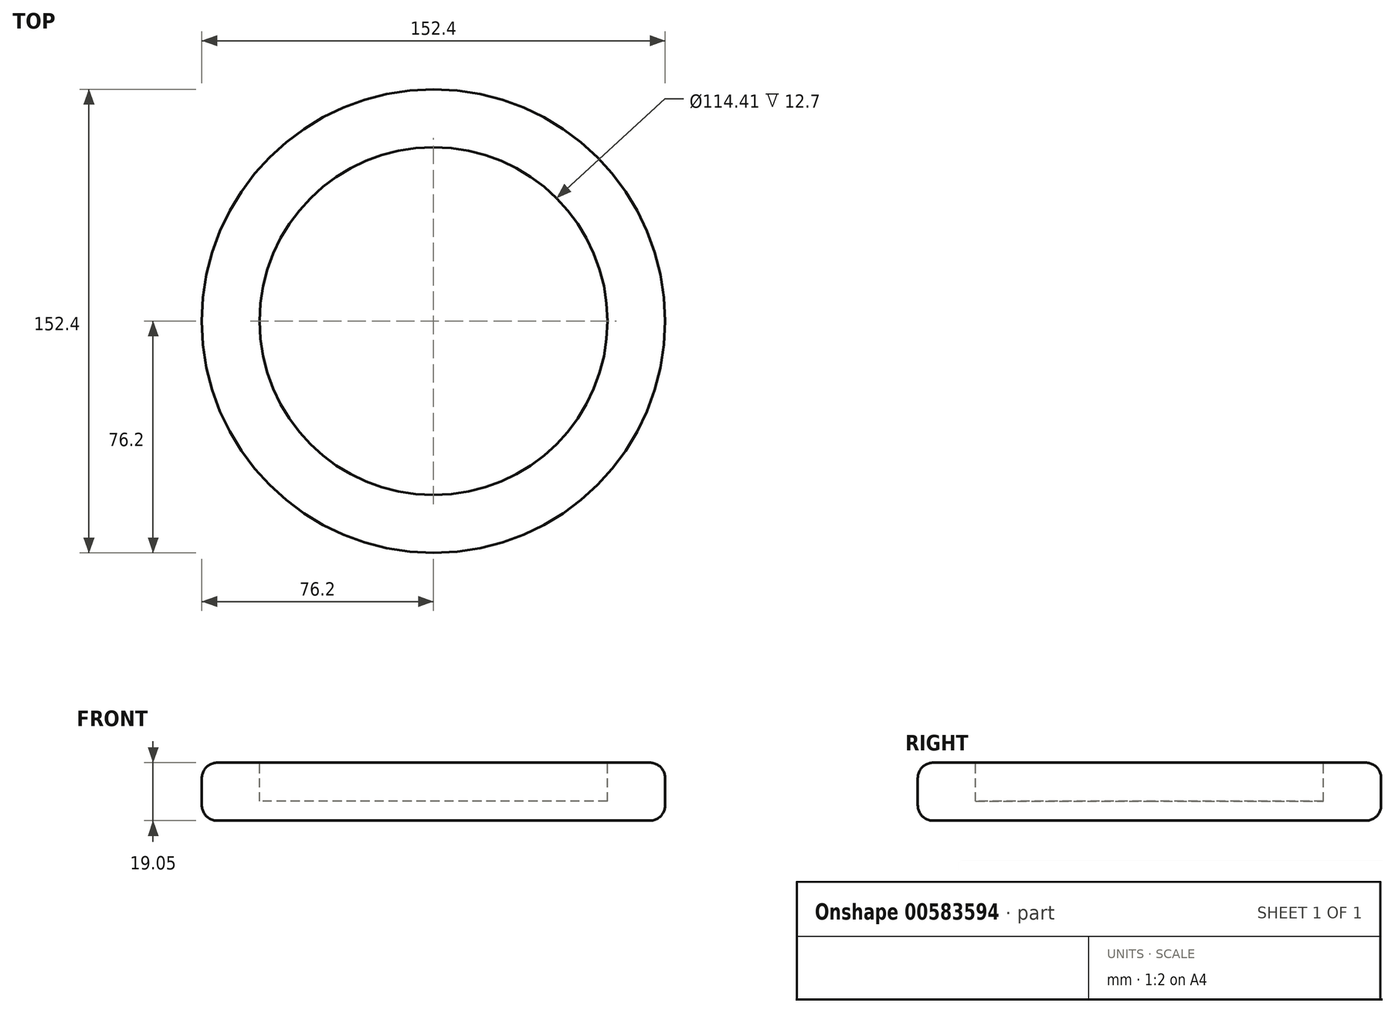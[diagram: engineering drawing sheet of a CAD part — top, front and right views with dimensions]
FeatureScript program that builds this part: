
annotation { "Feature Type Name" : "Feature", "Feature Type Description" : "" }
export const myFeature = defineFeature(function(context is Context, id is Id, definition is map)
    precondition{}
    {
        {
            var Q0;
            Q0=qCreatedBy(makeId("Top.planeOp"),FACE);
            var sketch = newSketch(context, id + "F0", { "sketchPlane" : qUnion([Q0])});
            skCircle(sketch, "E0", {"center": v(0, 0) * mm, "radius": 76.2 * mm});
            skSolve(sketch);
        }
        {
            var Q0;
            Q0 = qSketchRegion(id + "F0", true);
            extrude(context, id + "F1", {"entities" : qUnion([Q0]), "depth" : 19.05 * mm, "offsetDistance" : 25.4 * mm});
        }
        {
            var Q0;
            Q0=makeQuery(id+"F1.opExtrude","CAP_FACE",FACE,{"disambiguationData":[OSD([sQuery(id+"F0.wireOp",EDGE,"E0")])],"isStart":false});
            var sketch = newSketch(context, id + "F2", { "sketchPlane" : qUnion([Q0])});
            skCircle(sketch, "E1", {"center": v(0, 0) * mm, "radius": 57.2 * mm});
            skSolve(sketch);
        }
        {
            var Q0;
            Q0 = qSketchRegion(id + "F2", true);
            extrude(context, id + "F3", {"entities" : qUnion([Q0]), "operationType" : NewBodyOperationType.REMOVE, "oppositeDirection" : true, "depth" : 12.7 * mm, "offsetDistance" : 25.4 * mm});
        }
        {
            var Q0;
            Q0=makeQuery(id+"F3.boolean.opBoolean","COPY",EDGE,{"derivedFrom":makeQuery(id+"F3.opExtrude","CAP_EDGE",EDGE,{"disambiguationData":[OSD([sQuery(id+"F2.wireOp",EDGE,"E1")])],"isStart":true})});
            var Q1;
            Q1=makeQuery(id+"F1.opExtrude","CAP_EDGE",EDGE,{"disambiguationData":[OSD([sQuery(id+"F0.wireOp",EDGE,"E0")])],"isStart":false});
            fillet(context, id + "F4", {"entities" : qUnion([Q0, Q1]), "radius" : 5.08 * mm, "tangentPropagation" : true, "allowEdgeOverflow" : false});
        }
        {
            var Q0;
            Q0=makeQuery(id+"F1.opExtrude","CAP_EDGE",EDGE,{"disambiguationData":[OSD([sQuery(id+"F0.wireOp",EDGE,"E0")])],"isStart":true});
            fillet(context, id + "F5", {"entities" : qUnion([Q0]), "radius" : 5.08 * mm, "tangentPropagation" : true, "allowEdgeOverflow" : false});
        }
    });
